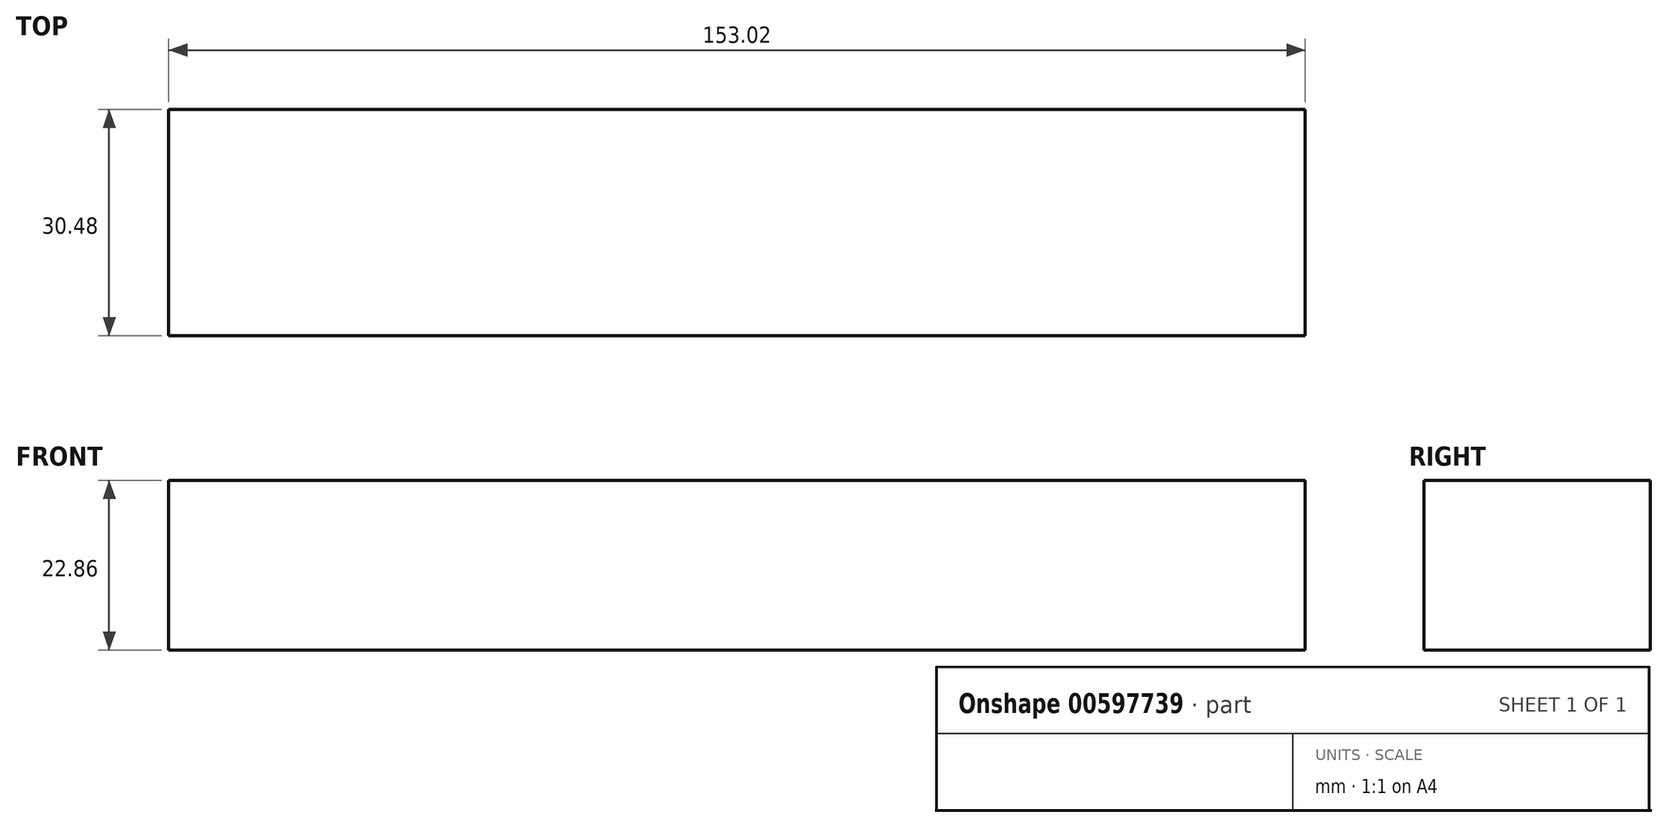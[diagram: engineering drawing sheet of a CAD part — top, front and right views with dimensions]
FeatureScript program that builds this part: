
annotation { "Feature Type Name" : "Feature", "Feature Type Description" : "" }
export const myFeature = defineFeature(function(context is Context, id is Id, definition is map)
    precondition{}
    {
        {
            var Q0;
            Q0=qCreatedBy(makeId("Front.planeOp"),FACE);
            var sketch = newSketch(context, id + "F0", { "sketchPlane" : qUnion([Q0])});
            skLineSegment(sketch, "E0.bottom", {"start": v(-76.51, 22.86) * mm, "end": v(76.51, 22.86) * mm});
            skLineSegment(sketch, "E0.top", {"start": v(-76.51, 0) * mm, "end": v(76.51, 0) * mm});
            skLineSegment(sketch, "E0.left", {"start": v(-76.51, 22.86) * mm, "end": v(-76.51, 0) * mm});
            skLineSegment(sketch, "E0.right", {"start": v(76.51, 22.86) * mm, "end": v(76.51, 0) * mm});
            skSolve(sketch);
        }
        {
            var Q0;
            Q0=makeQuery(id+"F0.imprint","IMPRINT",FACE,{"disambiguationData":[TD([[makeQuery(id+"F0.imprint","IMPRINT",EDGE,{"derivedFrom":sQuery(id+"F0.wireOp",EDGE,"E0.bottom")}),-1.0]])]});
            extrude(context, id + "F1", {"entities" : qUnion([Q0]), "depth" : 30.48 * mm, "offsetDistance" : 25.4 * mm});
        }
    });
